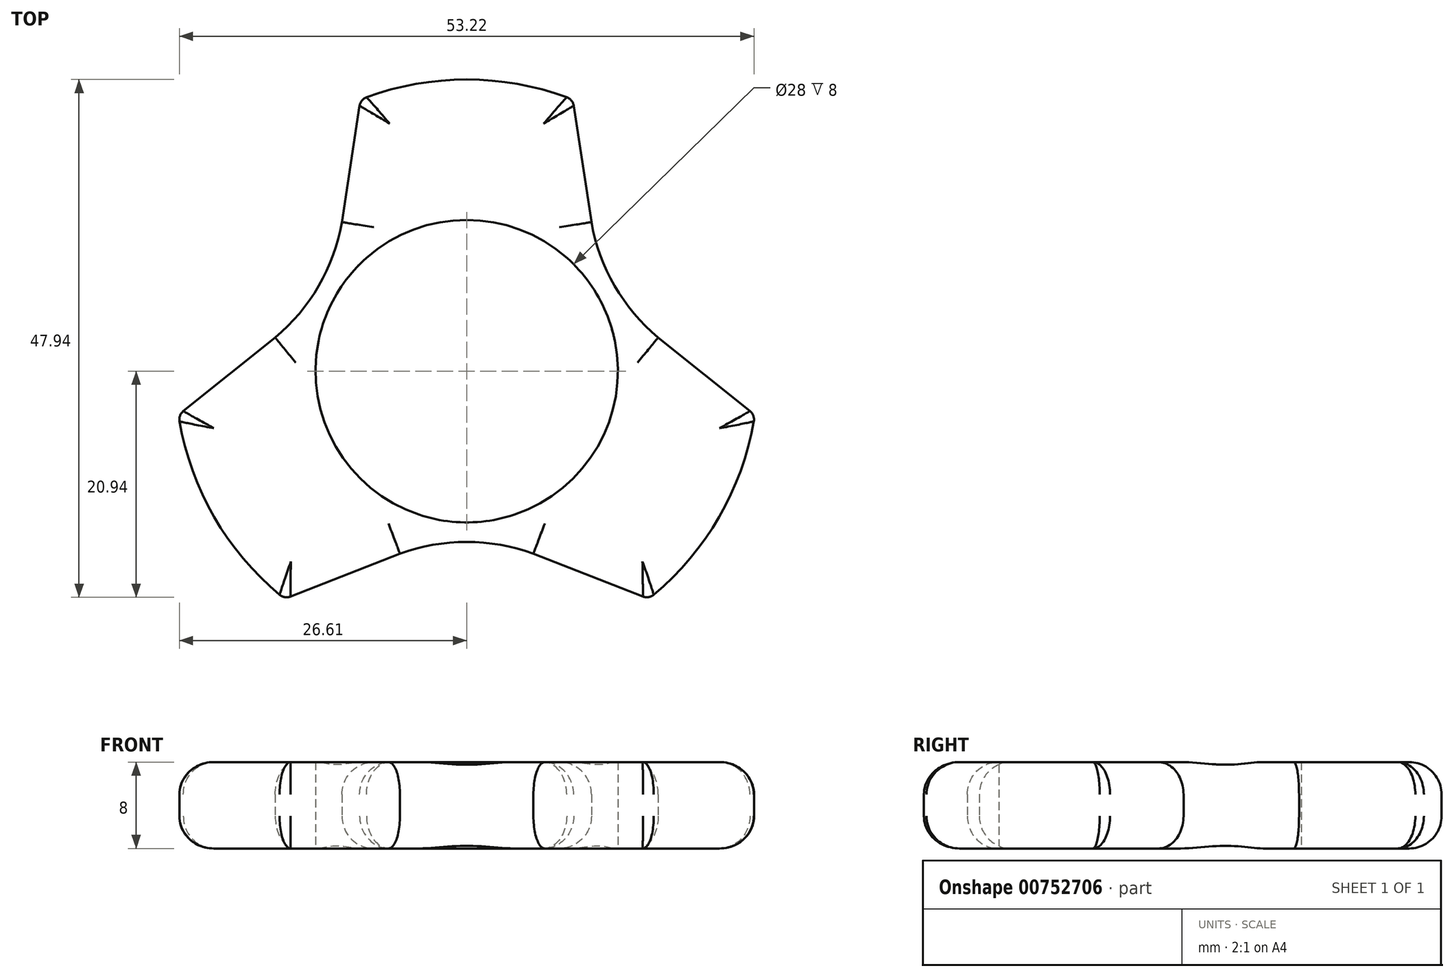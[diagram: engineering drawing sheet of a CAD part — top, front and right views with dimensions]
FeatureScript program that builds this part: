
annotation { "Feature Type Name" : "Feature", "Feature Type Description" : "" }
export const myFeature = defineFeature(function(context is Context, id is Id, definition is map)
    precondition{}
    {
        {
            var Q0;
            Q0=qCreatedBy(makeId("Top.planeOp"),FACE);
            var sketch = newSketch(context, id + "F0", { "sketchPlane" : qUnion([Q0])});
            skArc(sketch, "E0", {"start": v(9.83, 25.15) * mm, "mid": v(0, 27) * mm, "end": v(-9.83, 25.15) * mm});
            skArc(sketch, "E1.cCircle", {"start": v(9.83, 25.15) * mm, "mid": v(0, 27) * mm, "end": v(-9.83, 25.15) * mm, "construction": true});
            skLineSegment(sketch, "E2.0", {"start": v(9.83, 25.15) * mm, "end": v(11.55, 13.8) * mm});
            skLineSegment(sketch, "E2.1", {"start": v(16.87, -21.08) * mm, "end": v(6.18, -16.9) * mm});
            skLineSegment(sketch, "E2.2", {"start": v(-26.7, -4.06) * mm, "end": v(-17.73, 3.1) * mm});
            skArc(sketch, "E3.trimOffspring", {"start": v(-26.7, -4.06) * mm, "mid": v(-23.38, -13.5) * mm, "end": v(-16.87, -21.08) * mm});
            skArc(sketch, "E4.trimOffspring", {"start": v(16.87, -21.08) * mm, "mid": v(23.38, -13.5) * mm, "end": v(26.7, -4.06) * mm});
            skLineSegment(sketch, "E5.trimOffspring", {"start": v(-6.18, -16.9) * mm, "end": v(-16.87, -21.08) * mm});
            skLineSegment(sketch, "E6.trimOffspring", {"start": v(17.73, 3.1) * mm, "end": v(26.7, -4.06) * mm});
            skLineSegment(sketch, "E7.trimOffspring", {"start": v(-11.55, 13.8) * mm, "end": v(-9.83, 25.15) * mm});
            skCircle(sketch, "E8", {"center": v(0, 0) * mm, "radius": 14 * mm});
            skArc(sketch, "E9.MirrorCS", {"start": v(17.73, 3.1) * mm, "mid": v(13.7, 7.9) * mm, "end": v(11.55, 13.8) * mm});
            skArc(sketch, "E10.1.0", {"start": v(-11.55, 13.8) * mm, "mid": v(-13.7, 7.9) * mm, "end": v(-17.73, 3.1) * mm});
            skArc(sketch, "E10.2.0", {"start": v(-6.18, -16.9) * mm, "mid": v(0, -15.81) * mm, "end": v(6.18, -16.9) * mm});
            skSolve(sketch);
        }
        {
            var Q0;
            Q0=makeQuery(id+"F0.imprint","IMPRINT",FACE,{"disambiguationData":[TD([[makeQuery(id+"F0.imprint","IMPRINT",EDGE,{"derivedFrom":sQuery(id+"F0.wireOp",EDGE,"E0")}),1.0]])]});
            extrude(context, id + "F1", {"entities" : qUnion([Q0]), "depth" : 4 * mm, "offsetDistance" : 25 * mm, "hasSecondDirection" : true, "secondDirectionOppositeDirection" : true, "secondDirectionDepth" : 4 * mm});
        }
        {
            var Q0;
            Q0=makeQuery(id+"F1.opExtrude","CAP_EDGE",EDGE,{"disambiguationData":[OSD([sQuery(id+"F0.wireOp",EDGE,"hB14oN9n-8kFj-Rz35-B9qi-zIKxklWgJF2J")])],"isStart":false});
            var Q1;
            Q1=makeQuery(id+"F1.opExtrude","CAP_EDGE",EDGE,{"disambiguationData":[OSD([sQuery(id+"F0.wireOp",EDGE,"E2.1")])],"isStart":false});
            var Q2;
            Q2=makeQuery(id+"F1.opExtrude","CAP_EDGE",EDGE,{"disambiguationData":[OSD([sQuery(id+"F0.wireOp",EDGE,"E5.trimOffspring")])],"isStart":false});
            var Q3;
            Q3=makeQuery(id+"F1.opExtrude","CAP_EDGE",EDGE,{"disambiguationData":[OSD([sQuery(id+"F0.wireOp",EDGE,"E5.trimOffspring")])],"isStart":true});
            var Q4;
            Q4=makeQuery(id+"F1.opExtrude","CAP_EDGE",EDGE,{"disambiguationData":[OSD([sQuery(id+"F0.wireOp",EDGE,"hB14oN9n-8kFj-Rz35-B9qi-zIKxklWgJF2J")])],"isStart":true});
            var Q5;
            Q5=makeQuery(id+"F1.opExtrude","CAP_EDGE",EDGE,{"disambiguationData":[OSD([sQuery(id+"F0.wireOp",EDGE,"E2.1")])],"isStart":true});
            var Q6;
            Q6=makeQuery(id+"F1.opExtrude","CAP_EDGE",EDGE,{"disambiguationData":[OSD([sQuery(id+"F0.wireOp",EDGE,"E4.trimOffspring")])],"isStart":false});
            var Q7;
            Q7=makeQuery(id+"F1.opExtrude","CAP_EDGE",EDGE,{"disambiguationData":[OSD([sQuery(id+"F0.wireOp",EDGE,"E4.trimOffspring")])],"isStart":true});
            var Q8;
            Q8=makeQuery(id+"F1.opExtrude","CAP_EDGE",EDGE,{"disambiguationData":[OSD([sQuery(id+"F0.wireOp",EDGE,"E3.trimOffspring")])],"isStart":false});
            var Q9;
            Q9=makeQuery(id+"F1.opExtrude","CAP_EDGE",EDGE,{"disambiguationData":[OSD([sQuery(id+"F0.wireOp",EDGE,"E3.trimOffspring")])],"isStart":true});
            var Q10;
            Q10=makeQuery(id+"F1.opExtrude","CAP_EDGE",EDGE,{"disambiguationData":[OSD([sQuery(id+"F0.wireOp",EDGE,"98780713-d088-4c99-bdf2-f1f3d39e4d9e.trimOffspring")])],"isStart":true});
            var Q11;
            Q11=makeQuery(id+"F1.opExtrude","CAP_EDGE",EDGE,{"disambiguationData":[OSD([sQuery(id+"F0.wireOp",EDGE,"E7.trimOffspring")])],"isStart":true});
            var Q12;
            Q12=makeQuery(id+"F1.opExtrude","CAP_EDGE",EDGE,{"disambiguationData":[OSD([sQuery(id+"F0.wireOp",EDGE,"E7.trimOffspring")])],"isStart":false});
            var Q13;
            Q13=makeQuery(id+"F1.opExtrude","CAP_EDGE",EDGE,{"disambiguationData":[OSD([sQuery(id+"F0.wireOp",EDGE,"98780713-d088-4c99-bdf2-f1f3d39e4d9e.trimOffspring")])],"isStart":false});
            var Q14;
            Q14=makeQuery(id+"F1.opExtrude","CAP_EDGE",EDGE,{"disambiguationData":[OSD([sQuery(id+"F0.wireOp",EDGE,"E0")])],"isStart":true});
            var Q15;
            Q15=makeQuery(id+"F1.opExtrude","CAP_EDGE",EDGE,{"disambiguationData":[OSD([sQuery(id+"F0.wireOp",EDGE,"E0")])],"isStart":false});
            var Q16;
            Q16=makeQuery(id+"F1.opExtrude","CAP_EDGE",EDGE,{"disambiguationData":[OSD([sQuery(id+"F0.wireOp",EDGE,"86ab5906-744f-4bcc-a7a9-9ec6f4dbbb85.trimOffspring")])],"isStart":false});
            var Q17;
            Q17=makeQuery(id+"F1.opExtrude","CAP_EDGE",EDGE,{"disambiguationData":[OSD([sQuery(id+"F0.wireOp",EDGE,"E2.0")])],"isStart":false});
            var Q18;
            Q18=makeQuery(id+"F1.opExtrude","CAP_EDGE",EDGE,{"disambiguationData":[OSD([sQuery(id+"F0.wireOp",EDGE,"E2.0")])],"isStart":true});
            var Q19;
            Q19=makeQuery(id+"F1.opExtrude","CAP_EDGE",EDGE,{"disambiguationData":[OSD([sQuery(id+"F0.wireOp",EDGE,"86ab5906-744f-4bcc-a7a9-9ec6f4dbbb85.trimOffspring")])],"isStart":true});
            var Q20;
            Q20=makeQuery(id+"F1.opExtrude","CAP_EDGE",EDGE,{"disambiguationData":[OSD([sQuery(id+"F0.wireOp",EDGE,"E6.trimOffspring")])],"isStart":false});
            var Q21;
            Q21=makeQuery(id+"F1.opExtrude","CAP_EDGE",EDGE,{"disambiguationData":[OSD([sQuery(id+"F0.wireOp",EDGE,"E6.trimOffspring")])],"isStart":true});
            var Q22;
            Q22=makeQuery(id+"F1.opExtrude","CAP_EDGE",EDGE,{"disambiguationData":[OSD([sQuery(id+"F0.wireOp",EDGE,"E2.2")])],"isStart":false});
            var Q23;
            Q23=makeQuery(id+"F1.opExtrude","CAP_EDGE",EDGE,{"disambiguationData":[OSD([sQuery(id+"F0.wireOp",EDGE,"E2.2")])],"isStart":true});
            fillet(context, id + "F2", {"entities" : qUnion([Q0, Q1, Q2, Q3, Q4, Q5, Q6, Q7, Q8, Q9, Q10, Q11, Q12, Q13, Q14, Q15, Q16, Q17, Q18, Q19, Q20, Q21, Q22, Q23]), "radius" : 3 * mm, "tangentPropagation" : true, "allowEdgeOverflow" : false});
        }
        {
            var Q0;
            Q0=makeQuery(id+"F2.opFillet","BLEND_EDGE",EDGE,{"blendedFrom":[makeQuery(id+"F1.opExtrude","CAP_EDGE",EDGE,{"disambiguationData":[OSD([sQuery(id+"F0.wireOp",EDGE,"E2.1")])],"isStart":false}),makeQuery(id+"F1.opExtrude","CAP_EDGE",EDGE,{"disambiguationData":[OSD([sQuery(id+"F0.wireOp",EDGE,"E4.trimOffspring")])],"isStart":false})],"blendedInto":[]});
            var Q1;
            Q1=makeQuery(id+"F2.opFillet","BLEND_EDGE",EDGE,{"blendedFrom":[makeQuery(id+"F1.opExtrude","CAP_EDGE",EDGE,{"disambiguationData":[OSD([sQuery(id+"F0.wireOp",EDGE,"E3.trimOffspring")])],"isStart":false}),makeQuery(id+"F1.opExtrude","CAP_EDGE",EDGE,{"disambiguationData":[OSD([sQuery(id+"F0.wireOp",EDGE,"E5.trimOffspring")])],"isStart":false})],"blendedInto":[]});
            var Q2;
            Q2=makeQuery(id+"F2.opFillet","BLEND_EDGE",EDGE,{"blendedFrom":[makeQuery(id+"F1.opExtrude","CAP_EDGE",EDGE,{"disambiguationData":[OSD([sQuery(id+"F0.wireOp",EDGE,"E2.2")])],"isStart":false}),makeQuery(id+"F1.opExtrude","CAP_EDGE",EDGE,{"disambiguationData":[OSD([sQuery(id+"F0.wireOp",EDGE,"E3.trimOffspring")])],"isStart":false})],"blendedInto":[]});
            var Q3;
            Q3=makeQuery(id+"F2.opFillet","BLEND_EDGE",EDGE,{"blendedFrom":[makeQuery(id+"F1.opExtrude","CAP_EDGE",EDGE,{"disambiguationData":[OSD([sQuery(id+"F0.wireOp",EDGE,"E0")])],"isStart":true}),makeQuery(id+"F1.opExtrude","CAP_EDGE",EDGE,{"disambiguationData":[OSD([sQuery(id+"F0.wireOp",EDGE,"E7.trimOffspring")])],"isStart":true})],"blendedInto":[]});
            var Q4;
            Q4=makeQuery(id+"F2.opFillet","BLEND_EDGE",EDGE,{"blendedFrom":[makeQuery(id+"F1.opExtrude","CAP_EDGE",EDGE,{"disambiguationData":[OSD([sQuery(id+"F0.wireOp",EDGE,"E0")])],"isStart":false}),makeQuery(id+"F1.opExtrude","CAP_EDGE",EDGE,{"disambiguationData":[OSD([sQuery(id+"F0.wireOp",EDGE,"E2.0")])],"isStart":false})],"blendedInto":[]});
            var Q5;
            Q5=makeQuery(id+"F2.opFillet","BLEND_EDGE",EDGE,{"blendedFrom":[makeQuery(id+"F1.opExtrude","CAP_EDGE",EDGE,{"disambiguationData":[OSD([sQuery(id+"F0.wireOp",EDGE,"E4.trimOffspring")])],"isStart":false}),makeQuery(id+"F1.opExtrude","CAP_EDGE",EDGE,{"disambiguationData":[OSD([sQuery(id+"F0.wireOp",EDGE,"E6.trimOffspring")])],"isStart":false})],"blendedInto":[]});
            fillet(context, id + "F3", {"entities" : qUnion([Q0, Q1, Q2, Q3, Q4, Q5]), "radius" : 1 * mm, "tangentPropagation" : true, "allowEdgeOverflow" : false});
        }
    });
